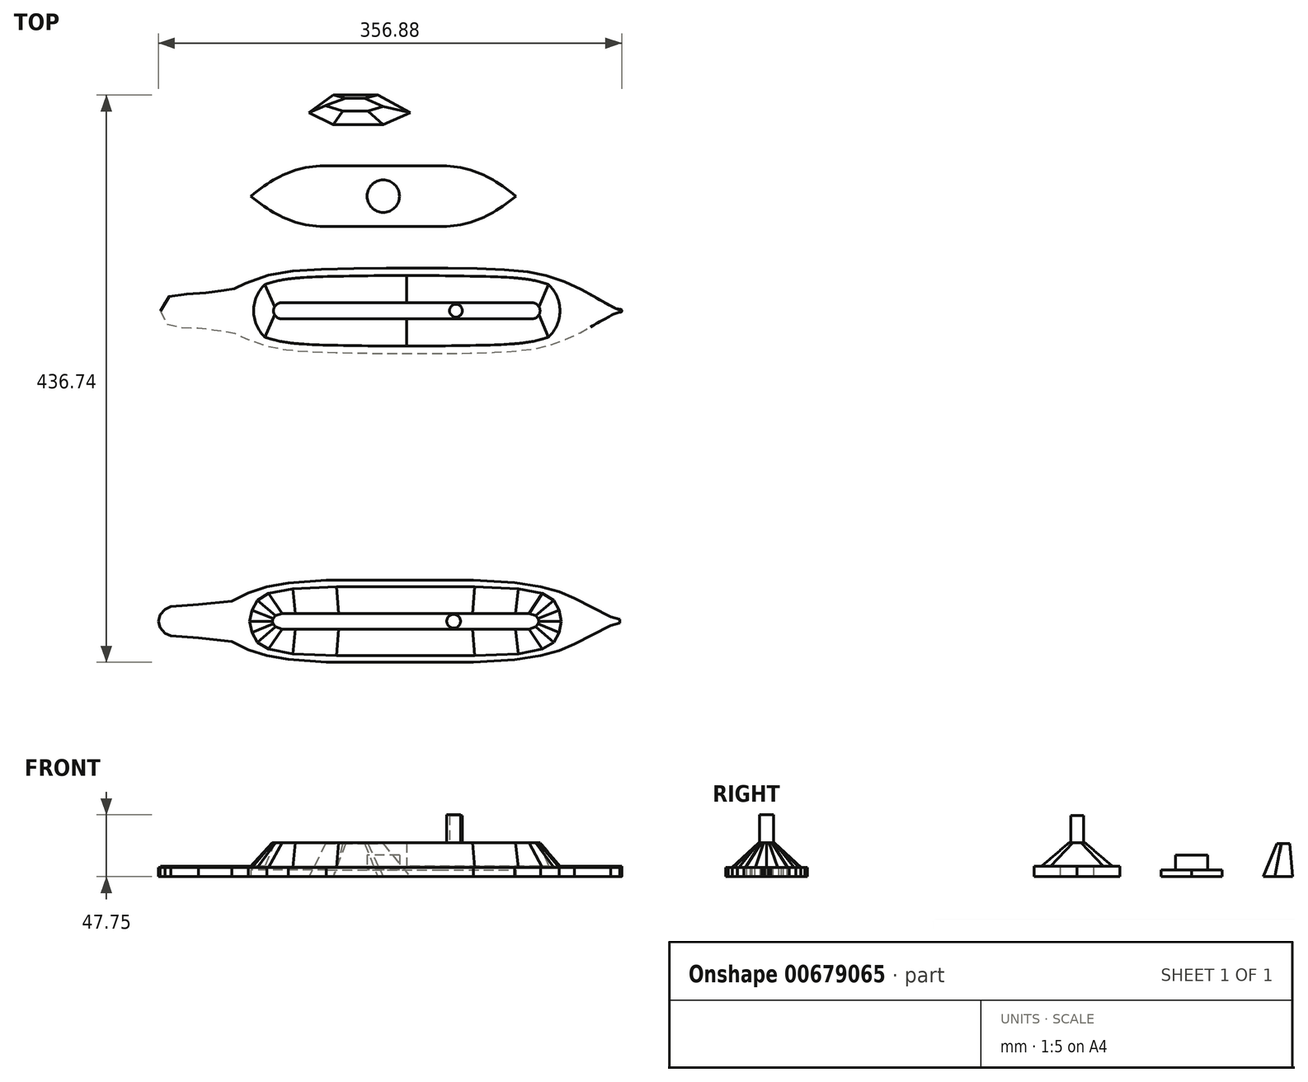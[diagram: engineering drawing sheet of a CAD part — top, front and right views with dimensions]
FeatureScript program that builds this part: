
annotation { "Feature Type Name" : "Feature", "Feature Type Description" : "" }
export const myFeature = defineFeature(function(context is Context, id is Id, definition is map)
    precondition{}
    {
        {
            var Q0;
            Q0=qCreatedBy(makeId("Top.planeOp"),FACE);
            var sketch = newSketch(context, id + "F0", { "sketchPlane" : qUnion([Q0])});
            skLineSegment(sketch, "E0", {"start": v(-42.94, 23.43) * mm, "end": v(0, 23.43) * mm});
            skFitSpline(sketch, "E1", {"points": [v(-42.94, 23.43) * mm, v(-102.11, 0) * mm], "startDerivative": vector(-68.76, 0) * mm, "endDerivative": vector(-60.63, -49.68) * mm});
            skLineSegment(sketch, "E2", {"start": v(-37.52, 23.43) * mm, "end": v(-119.82, 23.43) * mm, "construction": true});
            skLineSegment(sketch, "E3.MirrorCS", {"start": v(-42.94, -23.43) * mm, "end": v(0, -23.43) * mm});
            skFitSpline(sketch, "E4.MirrorCS", {"points": [v(-42.94, -23.43) * mm, v(-102.11, 0) * mm], "startDerivative": vector(-68.76, 0) * mm, "endDerivative": vector(-60.63, 49.68) * mm});
            skLineSegment(sketch, "E5.MirrorCS", {"start": v(42.94, 23.43) * mm, "end": v(0, 23.43) * mm});
            skFitSpline(sketch, "E6.MirrorCS", {"points": [v(42.94, 23.43) * mm, v(102.11, 0) * mm], "startDerivative": vector(68.76, 0) * mm, "endDerivative": vector(60.63, -49.68) * mm});
            skFitSpline(sketch, "E7.MirrorCS", {"points": [v(42.94, -23.43) * mm, v(102.11, 0) * mm], "startDerivative": vector(68.76, 0) * mm, "endDerivative": vector(60.63, 49.68) * mm});
            skLineSegment(sketch, "E8.MirrorCS", {"start": v(42.94, -23.43) * mm, "end": v(0, -23.43) * mm});
            skSolve(sketch);
        }
        {
            var Q0;
            Q0=makeQuery(id+"F0.imprint","IMPRINT",FACE,{"disambiguationData":[TD([[makeQuery(id+"F0.imprint","IMPRINT",EDGE,{"derivedFrom":sQuery(id+"F0.wireOp",EDGE,"E0")}),-1.0]])]});
            extrude(context, id + "F1", {"entities" : qUnion([Q0]), "depth" : 5.08 * mm, "offsetDistance" : 25.4 * mm});
        }
        {
            var Q0;
            Q0=makeQuery(id+"F1.opExtrude","CAP_FACE",FACE,{"disambiguationData":[OSD([sQuery(id+"F0.wireOp",EDGE,"E0"),sQuery(id+"F0.wireOp",EDGE,"E1"),sQuery(id+"F0.wireOp",EDGE,"E3.MirrorCS"),sQuery(id+"F0.wireOp",EDGE,"E4.MirrorCS"),sQuery(id+"F0.wireOp",EDGE,"E5.MirrorCS"),sQuery(id+"F0.wireOp",EDGE,"E6.MirrorCS"),sQuery(id+"F0.wireOp",EDGE,"E7.MirrorCS"),sQuery(id+"F0.wireOp",EDGE,"E8.MirrorCS")])],"isStart":false});
            var sketch = newSketch(context, id + "F2", { "sketchPlane" : qUnion([Q0])});
            skCircle(sketch, "E9", {"center": v(0, 0) * mm, "radius": 12.49 * mm});
            skSolve(sketch);
        }
        {
            var Q0;
            Q0=makeQuery(id+"F2.imprint","IMPRINT",FACE,{"disambiguationData":[TD([[makeQuery(id+"F2.imprint","IMPRINT",EDGE,{"derivedFrom":sQuery(id+"F2.wireOp",EDGE,"E9")}),1.0]])]});
            extrude(context, id + "F3", {"entities" : qUnion([Q0]), "operationType" : NewBodyOperationType.ADD, "depth" : 11.68 * mm, "offsetDistance" : 25.4 * mm});
        }
        {
            var Q0;
            Q0=qCreatedBy(makeId("Top.planeOp"),FACE);
            var sketch = newSketch(context, id + "F4", { "sketchPlane" : qUnion([Q0])});
            skLineSegment(sketch, "E10", {"start": v(-71.94, -45.48) * mm, "end": v(-71.94, -186.72) * mm, "construction": true});
            skLineSegment(sketch, "E11", {"start": v(108.08, -39.14) * mm, "end": v(108.08, -186.72) * mm, "construction": true});
            skLineSegment(sketch, "E12", {"start": v(-197.77, -88.3) * mm, "end": v(328.2, -88.3) * mm, "construction": true});
            skFitSpline(sketch, "E13", {"points": [v(-171.65, -88.3) * mm, v(-163.55, -76.65) * mm, v(-146.07, -75.28) * mm, v(-127.86, -73.29) * mm, v(-116.2, -71.5) * mm, v(-114.9, -71.28) * mm, v(-113.7, -70.6) * mm, v(-93.72, -62.34) * mm, v(-61.63, -57.06) * mm, v(-9.38, -55.61) * mm, v(41.39, -55.4) * mm, v(84.93, -56.24) * mm, v(114.66, -58.75) * mm, v(131.08, -62.76) * mm, v(149.8, -70.54) * mm, v(159.24, -75.62) * mm, v(168.52, -80.9) * mm, v(175.32, -84.67) * mm, v(180.3, -86.82) * mm, v(183.42, -87.51) * mm, v(183.64, -88.3) * mm], "startDerivative": vector(0, 395.34) * mm, "endDerivative": vector(-3.7, -98.79) * mm});
            skLineSegment(sketch, "E14", {"start": v(-171.65, -79.57) * mm, "end": v(-171.65, -98.9) * mm, "construction": true});
            skFitSpline(sketch, "E15.MirrorCS", {"points": [v(-171.65, -88.3) * mm, v(-163.55, -99.94) * mm, v(-146.07, -101.3) * mm, v(-127.86, -103.3) * mm, v(-116.2, -105.09) * mm, v(-114.9, -105.31) * mm, v(-113.7, -106) * mm, v(-93.72, -114.25) * mm, v(-61.63, -119.53) * mm, v(-9.38, -120.98) * mm, v(41.39, -121.2) * mm, v(84.93, -120.35) * mm, v(114.66, -117.84) * mm, v(131.08, -113.83) * mm, v(149.8, -106.05) * mm, v(159.24, -100.97) * mm, v(168.52, -95.69) * mm, v(175.32, -91.92) * mm, v(180.3, -89.77) * mm, v(183.42, -89.08) * mm, v(183.64, -88.3) * mm], "startDerivative": vector(0, -395.34) * mm, "endDerivative": vector(-3.7, 98.79) * mm});
            skSolve(sketch);
        }
        {
            var Q0;
            Q0=makeQuery(id+"F4.imprint","IMPRINT",FACE,{"disambiguationData":[TD([[makeQuery(id+"F4.imprint","IMPRINT",EDGE,{"derivedFrom":sQuery(id+"F4.wireOp",EDGE,"E13")}),-1.0]])]});
            extrude(context, id + "F5", {"entities" : qUnion([Q0]), "depth" : 8.13 * mm, "offsetDistance" : 25.4 * mm});
        }
        {
            var Q0;
            Q0=makeQuery(id+"F5.opExtrude","CAP_FACE",FACE,{"disambiguationData":[OSD([sQuery(id+"F4.wireOp",EDGE,"E13"),sQuery(id+"F4.wireOp",EDGE,"E15.MirrorCS")])],"isStart":false});
            var sketch = newSketch(context, id + "F6", { "sketchPlane" : qUnion([Q0])});
            skLineSegment(sketch, "E16.0", {"start": v(-71.94, -45.48) * mm, "end": v(-71.94, -186.72) * mm, "construction": true});
            skLineSegment(sketch, "E17.0", {"start": v(108.08, -39.14) * mm, "end": v(108.08, -186.72) * mm, "construction": true});
            skLineSegment(sketch, "E18.0", {"start": v(-197.77, -88.3) * mm, "end": v(328.2, -88.3) * mm, "construction": true});
            skArc(sketch, "E19", {"start": v(-60.92, -62.61) * mm, "mid": v(-99.9, -88.3) * mm, "end": v(-60.92, -113.98) * mm});
            skArc(sketch, "E20", {"start": v(97.06, -113.98) * mm, "mid": v(102.46, -115.67) * mm, "end": v(108.08, -116.24) * mm});
            skFitSpline(sketch, "E21", {"points": [v(-109.29, -75.39) * mm, v(-83.95, -65.87) * mm, v(-65.76, -63) * mm, v(-41.52, -61.82) * mm, v(18.07, -61.25) * mm], "startDerivative": vector(81.3, 42.56) * mm, "endDerivative": vector(39.77, -2.18) * mm});
            skLineSegment(sketch, "E22", {"start": v(18.07, -51.14) * mm, "end": v(18.07, -141.86) * mm, "construction": true});
            skLineSegment(sketch, "E23", {"start": v(-71.94, -51.14) * mm, "end": v(108.08, -51.14) * mm, "construction": true});
            skFitSpline(sketch, "E24.MirrorCS", {"points": [v(145.42, -75.39) * mm, v(120.09, -65.87) * mm, v(101.9, -63) * mm, v(77.66, -61.82) * mm, v(18.07, -61.25) * mm], "startDerivative": vector(-81.3, 42.56) * mm, "endDerivative": vector(-39.77, -2.18) * mm});
            skLineSegment(sketch, "E25.MirrorCS", {"start": v(233.9, -88.3) * mm, "end": v(-292.06, -88.3) * mm, "construction": true});
            skFitSpline(sketch, "E26.MirrorCS", {"points": [v(-109.29, -101.2) * mm, v(-83.95, -110.72) * mm, v(-65.76, -113.6) * mm, v(-41.52, -114.77) * mm, v(18.07, -115.34) * mm], "startDerivative": vector(81.3, -42.56) * mm, "endDerivative": vector(39.77, 2.18) * mm});
            skFitSpline(sketch, "E27.MirrorCS", {"points": [v(145.42, -101.2) * mm, v(120.09, -110.72) * mm, v(101.9, -113.6) * mm, v(77.66, -114.77) * mm, v(18.07, -115.34) * mm], "startDerivative": vector(-81.3, -42.56) * mm, "endDerivative": vector(-39.77, 2.18) * mm});
            skArc(sketch, "E28.trimOffspring", {"start": v(108.08, -116.24) * mm, "mid": v(135.46, -82.67) * mm, "end": v(97.06, -62.61) * mm});
            skArc(sketch, "E29.trimOffspring", {"start": v(108.08, -60.35) * mm, "mid": v(102.46, -60.92) * mm, "end": v(97.06, -62.61) * mm});
            skLineSegment(sketch, "E30", {"start": v(145.42, -75.39) * mm, "end": v(145.42, -101.2) * mm});
            skLineSegment(sketch, "E31", {"start": v(-109.29, -75.39) * mm, "end": v(-109.29, -101.2) * mm});
            skSolve(sketch);
        }
        {
            var Q0;
            Q0=makeQuery(id+"F5.opExtrude","CAP_FACE",FACE,{"disambiguationData":[OSD([sQuery(id+"F4.wireOp",EDGE,"E13"),sQuery(id+"F4.wireOp",EDGE,"E15.MirrorCS")])],"isStart":false});
            cPlane(context, id + "F7", {"entities" : qUnion([Q0]), "cplaneType" : CPlaneType.OFFSET, "offset" : 18.03 * mm, "width" : 152.4 * mm, "height" : 152.4 * mm});
        }
        {
            var Q0;
            Q0=qCreatedBy(id+"F7.planeOp",FACE);
            var sketch = newSketch(context, id + "F8", { "sketchPlane" : qUnion([Q0])});
            skLineSegment(sketch, "E32.0", {"start": v(-197.77, -88.3) * mm, "end": v(328.2, -88.3) * mm, "construction": true});
            skArc(sketch, "E33", {"start": v(-78.37, -82.08) * mm, "mid": v(-84.59, -88.3) * mm, "end": v(-78.37, -94.5) * mm});
            skLineSegment(sketch, "E34.0", {"start": v(18.07, -51.14) * mm, "end": v(18.07, -141.86) * mm, "construction": true});
            skArc(sketch, "E35.MirrorC", {"start": v(114.51, -82.08) * mm, "mid": v(120.73, -88.3) * mm, "end": v(114.51, -94.5) * mm});
            skLineSegment(sketch, "E36.bottom", {"start": v(-78.37, -82.08) * mm, "end": v(114.51, -82.08) * mm});
            skLineSegment(sketch, "E36.top", {"start": v(-78.37, -94.5) * mm, "end": v(114.51, -94.5) * mm});
            skSolve(sketch);
        }
        {
            var Q0;
            Q0=sQuery(id+"F6.wireOp",VERTEX,"E21.1.internal");
            var Q1;
            Q1=sQuery(id+"F8.wireOp",VERTEX,"E33.start");
            var Q2;
            Q2=sQuery(id+"F6.wireOp",VERTEX,"E26.MirrorCS.1.internal");
            cPlane(context, id + "F9", {"entities" : qUnion([Q0, Q1, Q2]), "cplaneType" : CPlaneType.THREE_POINT, "offset" : 25.4 * mm, "width" : 152.4 * mm, "height" : 152.4 * mm});
        }
        {
            var Q0;
            Q0=qCreatedBy(id+"F9.planeOp",FACE);
            var sketch = newSketch(context, id + "F10", { "sketchPlane" : qUnion([Q0])});
            skLineSegment(sketch, "E37", {"start": v(94.5, 1.85) * mm, "end": v(110.72, -17.02) * mm});
            skLineSegment(sketch, "E38", {"start": v(82.08, 1.85) * mm, "end": v(65.87, -17.02) * mm});
            skSolve(sketch);
        }
        {
            var Q0;
            Q0=sQuery(id+"F8.wireOp",VERTEX,"E36.bottom.end");
            var Q1;
            Q1=sQuery(id+"F6.wireOp",VERTEX,"E24.MirrorCS.1.internal");
            var Q2;
            Q2=sQuery(id+"F6.wireOp",VERTEX,"E27.MirrorCS.1.internal");
            cPlane(context, id + "F11", {"entities" : qUnion([Q0, Q1, Q2]), "cplaneType" : CPlaneType.THREE_POINT, "offset" : 25.4 * mm, "width" : 152.4 * mm, "height" : 152.4 * mm});
        }
        {
            var Q0;
            Q0=qCreatedBy(id+"F11.planeOp",FACE);
            var sketch = newSketch(context, id + "F12", { "sketchPlane" : qUnion([Q0])});
            skLineSegment(sketch, "E39", {"start": v(-110.72, -27.7) * mm, "end": v(-94.5, -8.82) * mm});
            skLineSegment(sketch, "E40", {"start": v(-82.08, -8.82) * mm, "end": v(-65.87, -27.7) * mm});
            skSolve(sketch);
        }
        {
            var Q1;
            Q1=makeQuery(id+"F8.imprint","IMPRINT",FACE,{"disambiguationData":[TD([[makeQuery(id+"F8.imprint","IMPRINT",EDGE,{"derivedFrom":sQuery(id+"F8.wireOp",EDGE,"E33")}),1.0]])]});
            var Q2;
            {var subQ4=sQuery(id+"F6.wireOp",EDGE,"E21");var subQ5=sQuery(id+"F6.wireOp",EDGE,"E19");var subQ7=makeQuery(id+"F6.imprint","INTERSECT",VERTEX,{"disambiguationData":[OD(1.0)],"derivedFrom":[subQ5,subQ4]});Q2=makeQuery(id+"F6.imprint","IMPRINT",FACE,{"disambiguationData":[TD([[makeQuery(id+"F6.imprint","IMPRINT",EDGE,{"disambiguationData":[TD([[subQ7,-1.0]])],"derivedFrom":subQ5}),1.0]])]});}
            var Q3;
            Q3=sQuery(id+"F12.wireOp",EDGE,"E39");
            var Q4;
            Q4=sQuery(id+"F12.wireOp",EDGE,"E40");
            var Q5;
            Q5=sQuery(id+"F10.wireOp",EDGE,"E37");
            var Q6;
            Q6=sQuery(id+"F10.wireOp",EDGE,"E38");
            loft(context, id + "F13", {"operationType" : NewBodyOperationType.ADD, "addGuides" : true, "sheetProfilesArray" : [{ "sheetProfileEntities" : qUnion([Q1]) }, { "sheetProfileEntities" : qUnion([Q2]) }], "guidesArray" : [{ "guideEntities" : qUnion([Q3]), "guideDerivativeType" : LoftGuideDerivativeType.DEFAULT, "guideDerivativeMagnitude" : 1 }, { "guideEntities" : qUnion([Q4]), "guideDerivativeType" : LoftGuideDerivativeType.DEFAULT, "guideDerivativeMagnitude" : 1 }, { "guideEntities" : qUnion([Q5]), "guideDerivativeType" : LoftGuideDerivativeType.DEFAULT, "guideDerivativeMagnitude" : 1 }, { "guideEntities" : qUnion([Q6]), "guideDerivativeType" : LoftGuideDerivativeType.DEFAULT, "guideDerivativeMagnitude" : 1 }]});
        }
        {
            var Q0;
            Q0=makeQuery(id+"F8.imprint","IMPRINT",FACE,{"disambiguationData":[TD([[makeQuery(id+"F8.imprint","IMPRINT",EDGE,{"derivedFrom":sQuery(id+"F8.wireOp",EDGE,"E33")}),1.0]])]});
            var sketch = newSketch(context, id + "F14", { "sketchPlane" : qUnion([Q0])});
            skCircle(sketch, "E41", {"center": v(55.96, -88.24) * mm, "radius": 4.95 * mm});
            skSolve(sketch);
        }
        {
            var Q0;
            Q0=makeQuery(id+"F14.imprint","IMPRINT",FACE,{"disambiguationData":[TD([[makeQuery(id+"F14.imprint","IMPRINT",EDGE,{"derivedFrom":sQuery(id+"F14.wireOp",EDGE,"E41")}),1.0]])]});
            extrude(context, id + "F15", {"entities" : qUnion([Q0]), "operationType" : NewBodyOperationType.ADD, "depth" : 21.08 * mm, "offsetDistance" : 25.4 * mm});
        }
        {
            var Q0;
            Q0=qCreatedBy(makeId("Top.planeOp"),FACE);
            var sketch = newSketch(context, id + "F16", { "sketchPlane" : qUnion([Q0])});
            skLineSegment(sketch, "E42", {"start": v(-57.17, 64.26) * mm, "end": v(-38.38, 77.84) * mm});
            skLineSegment(sketch, "E43", {"start": v(-38.38, 77.84) * mm, "end": v(-4.18, 77.84) * mm});
            skLineSegment(sketch, "E44", {"start": v(-4.18, 77.84) * mm, "end": v(20.88, 64.26) * mm});
            skLineSegment(sketch, "E45", {"start": v(20.88, 64.26) * mm, "end": v(0, 55.13) * mm});
            skLineSegment(sketch, "E46", {"start": v(0, 55.13) * mm, "end": v(-38.38, 55.13) * mm});
            skLineSegment(sketch, "E47", {"start": v(-38.38, 55.13) * mm, "end": v(-57.17, 64.26) * mm});
            skSolve(sketch);
        }
        {
            var Q0;
            Q0=makeQuery(id+"F16.imprint","IMPRINT",FACE,{"disambiguationData":[TD([[makeQuery(id+"F16.imprint","IMPRINT",EDGE,{"derivedFrom":sQuery(id+"F16.wireOp",EDGE,"E42")}),-1.0]])]});
            cPlane(context, id + "F17", {"entities" : qUnion([Q0]), "cplaneType" : CPlaneType.OFFSET, "offset" : 25.4 * mm, "width" : 152.4 * mm, "height" : 152.4 * mm});
        }
        {
            var Q0;
            Q0=qCreatedBy(id+"F17.planeOp",FACE);
            var sketch = newSketch(context, id + "F18", { "sketchPlane" : qUnion([Q0])});
            skLineSegment(sketch, "E48", {"start": v(-29.05, 75.27) * mm, "end": v(-44.41, 69.77) * mm});
            skLineSegment(sketch, "E49", {"start": v(-44.41, 69.77) * mm, "end": v(-31.25, 65.58) * mm});
            skLineSegment(sketch, "E50", {"start": v(-31.25, 65.58) * mm, "end": v(-11.87, 65.58) * mm});
            skLineSegment(sketch, "E51", {"start": v(-11.87, 65.58) * mm, "end": v(0, 68.93) * mm});
            skLineSegment(sketch, "E52", {"start": v(0, 68.93) * mm, "end": v(-14.39, 75.38) * mm});
            skLineSegment(sketch, "E53", {"start": v(-14.39, 75.38) * mm, "end": v(-29.05, 75.27) * mm});
            skSolve(sketch);
        }
        {
            var Q0;
            Q0=makeQuery(id+"F18.imprint","IMPRINT",FACE,{"disambiguationData":[TD([[makeQuery(id+"F18.imprint","IMPRINT",EDGE,{"derivedFrom":sQuery(id+"F18.wireOp",EDGE,"E48")}),1.0]])]});
            var Q1;
            Q1=makeQuery(id+"F16.imprint","IMPRINT",FACE,{"disambiguationData":[TD([[makeQuery(id+"F16.imprint","IMPRINT",EDGE,{"derivedFrom":sQuery(id+"F16.wireOp",EDGE,"E42")}),-1.0]])]});
            loft(context, id + "F19", {"sheetProfilesArray" : [{ "sheetProfileEntities" : qUnion([Q0]) }, { "sheetProfileEntities" : qUnion([Q1]) }]});
        }
        {
            var Q0;
            Q0=qCreatedBy(makeId("Top.planeOp"),FACE);
            var sketch = newSketch(context, id + "F20", { "sketchPlane" : qUnion([Q0])});
            skLineSegment(sketch, "E54", {"start": v(-176.14, -327.4) * mm, "end": v(194.44, -327.4) * mm, "construction": true});
            skLineSegment(sketch, "E55", {"start": v(-173.24, -327.4) * mm, "end": v(-171.72, -322.5) * mm});
            skLineSegment(sketch, "E56", {"start": v(-171.72, -322.5) * mm, "end": v(-167.99, -318.24) * mm});
            skLineSegment(sketch, "E57", {"start": v(-167.99, -318.24) * mm, "end": v(-163.53, -316.13) * mm});
            skLineSegment(sketch, "E58", {"start": v(-163.53, -316.13) * mm, "end": v(-142.23, -314.57) * mm});
            skLineSegment(sketch, "E59", {"start": v(-142.23, -314.57) * mm, "end": v(-116.78, -311.82) * mm});
            skLineSegment(sketch, "E60", {"start": v(-116.78, -311.82) * mm, "end": v(-104, -305.48) * mm});
            skLineSegment(sketch, "E61", {"start": v(-104, -305.48) * mm, "end": v(-89.78, -300.98) * mm});
            skLineSegment(sketch, "E62", {"start": v(-89.78, -300.98) * mm, "end": v(-73.04, -298.02) * mm});
            skLineSegment(sketch, "E63", {"start": v(-73.04, -298.02) * mm, "end": v(-43.76, -295.9) * mm});
            skLineSegment(sketch, "E64", {"start": v(-43.76, -295.9) * mm, "end": v(69.46, -295.9) * mm});
            skLineSegment(sketch, "E65", {"start": v(69.46, -295.9) * mm, "end": v(101.23, -297.81) * mm});
            skLineSegment(sketch, "E66", {"start": v(101.23, -297.81) * mm, "end": v(121.16, -300.98) * mm});
            skLineSegment(sketch, "E67", {"start": v(121.16, -300.98) * mm, "end": v(135.46, -304.73) * mm});
            skLineSegment(sketch, "E68", {"start": v(135.46, -304.73) * mm, "end": v(147.24, -309.84) * mm});
            skLineSegment(sketch, "E69", {"start": v(147.24, -309.84) * mm, "end": v(157.53, -315.1) * mm});
            skLineSegment(sketch, "E70", {"start": v(157.53, -315.1) * mm, "end": v(175.12, -324.06) * mm});
            skLineSegment(sketch, "E71", {"start": v(175.12, -324.06) * mm, "end": v(182.27, -325.93) * mm});
            skLineSegment(sketch, "E72", {"start": v(182.27, -325.93) * mm, "end": v(182.27, -327.4) * mm});
            skLineSegment(sketch, "E73.MirrorCS", {"start": v(-73.04, -356.78) * mm, "end": v(-43.76, -358.9) * mm});
            skLineSegment(sketch, "E74.MirrorCS", {"start": v(-89.78, -353.82) * mm, "end": v(-73.04, -356.78) * mm});
            skLineSegment(sketch, "E75.MirrorCS", {"start": v(-104, -349.32) * mm, "end": v(-89.78, -353.82) * mm});
            skLineSegment(sketch, "E76.MirrorCS", {"start": v(-116.78, -342.98) * mm, "end": v(-104, -349.32) * mm});
            skLineSegment(sketch, "E77.MirrorCS", {"start": v(-142.23, -340.23) * mm, "end": v(-116.78, -342.98) * mm});
            skLineSegment(sketch, "E78.MirrorCS", {"start": v(-163.53, -338.67) * mm, "end": v(-142.23, -340.23) * mm});
            skLineSegment(sketch, "E79.MirrorCS", {"start": v(-167.99, -336.56) * mm, "end": v(-163.53, -338.67) * mm});
            skLineSegment(sketch, "E80.MirrorCS", {"start": v(-173.24, -327.4) * mm, "end": v(-171.72, -332.3) * mm});
            skLineSegment(sketch, "E81.MirrorCS", {"start": v(-171.72, -332.3) * mm, "end": v(-167.99, -336.56) * mm});
            skLineSegment(sketch, "E82.MirrorCS", {"start": v(-43.76, -358.9) * mm, "end": v(69.46, -358.9) * mm});
            skLineSegment(sketch, "E83.MirrorCS", {"start": v(69.46, -358.9) * mm, "end": v(101.23, -357) * mm});
            skLineSegment(sketch, "E84.MirrorCS", {"start": v(101.23, -357) * mm, "end": v(121.16, -353.82) * mm});
            skLineSegment(sketch, "E85.MirrorCS", {"start": v(121.16, -353.82) * mm, "end": v(135.46, -350.07) * mm});
            skLineSegment(sketch, "E86.MirrorCS", {"start": v(135.46, -350.07) * mm, "end": v(147.24, -344.96) * mm});
            skLineSegment(sketch, "E87.MirrorCS", {"start": v(147.24, -344.96) * mm, "end": v(157.53, -339.7) * mm});
            skLineSegment(sketch, "E88.MirrorCS", {"start": v(157.53, -339.7) * mm, "end": v(175.12, -330.74) * mm});
            skLineSegment(sketch, "E89.MirrorCS", {"start": v(175.12, -330.74) * mm, "end": v(182.27, -328.87) * mm});
            skLineSegment(sketch, "E90.MirrorCS", {"start": v(182.27, -328.87) * mm, "end": v(182.27, -327.4) * mm});
            skSolve(sketch);
        }
        {
            var Q0;
            Q0=makeQuery(id+"F20.imprint","IMPRINT",FACE,{"disambiguationData":[TD([[makeQuery(id+"F20.imprint","IMPRINT",EDGE,{"derivedFrom":sQuery(id+"F20.wireOp",EDGE,"E55")}),-1.0]])]});
            extrude(context, id + "F21", {"entities" : qUnion([Q0]), "depth" : 7.11 * mm, "offsetDistance" : 25.4 * mm});
        }
        {
            var Q0;
            Q0=makeQuery(id+"F21.opExtrude","CAP_FACE",FACE,{"disambiguationData":[OSD([sQuery(id+"F20.wireOp",EDGE,"E55"),sQuery(id+"F20.wireOp",EDGE,"E56"),sQuery(id+"F20.wireOp",EDGE,"E57"),sQuery(id+"F20.wireOp",EDGE,"E58"),sQuery(id+"F20.wireOp",EDGE,"E59"),sQuery(id+"F20.wireOp",EDGE,"E60"),sQuery(id+"F20.wireOp",EDGE,"E61"),sQuery(id+"F20.wireOp",EDGE,"E62"),sQuery(id+"F20.wireOp",EDGE,"E63"),sQuery(id+"F20.wireOp",EDGE,"E64"),sQuery(id+"F20.wireOp",EDGE,"E65"),sQuery(id+"F20.wireOp",EDGE,"E66"),sQuery(id+"F20.wireOp",EDGE,"E67"),sQuery(id+"F20.wireOp",EDGE,"E68"),sQuery(id+"F20.wireOp",EDGE,"E69"),sQuery(id+"F20.wireOp",EDGE,"E70"),sQuery(id+"F20.wireOp",EDGE,"E71"),sQuery(id+"F20.wireOp",EDGE,"E72"),sQuery(id+"F20.wireOp",EDGE,"E73.MirrorCS"),sQuery(id+"F20.wireOp",EDGE,"E74.MirrorCS"),sQuery(id+"F20.wireOp",EDGE,"E75.MirrorCS"),sQuery(id+"F20.wireOp",EDGE,"E76.MirrorCS"),sQuery(id+"F20.wireOp",EDGE,"E77.MirrorCS"),sQuery(id+"F20.wireOp",EDGE,"E78.MirrorCS"),sQuery(id+"F20.wireOp",EDGE,"E79.MirrorCS"),sQuery(id+"F20.wireOp",EDGE,"E80.MirrorCS"),sQuery(id+"F20.wireOp",EDGE,"E81.MirrorCS"),sQuery(id+"F20.wireOp",EDGE,"E82.MirrorCS"),sQuery(id+"F20.wireOp",EDGE,"E83.MirrorCS"),sQuery(id+"F20.wireOp",EDGE,"E84.MirrorCS"),sQuery(id+"F20.wireOp",EDGE,"E85.MirrorCS"),sQuery(id+"F20.wireOp",EDGE,"E86.MirrorCS"),sQuery(id+"F20.wireOp",EDGE,"E87.MirrorCS"),sQuery(id+"F20.wireOp",EDGE,"E88.MirrorCS"),sQuery(id+"F20.wireOp",EDGE,"E89.MirrorCS"),sQuery(id+"F20.wireOp",EDGE,"E90.MirrorCS")])],"isStart":false});
            var sketch = newSketch(context, id + "F22", { "sketchPlane" : qUnion([Q0])});
            skLineSegment(sketch, "E91.0", {"start": v(-176.14, -327.4) * mm, "end": v(194.44, -327.4) * mm, "construction": true});
            skLineSegment(sketch, "E92", {"start": v(-102.83, -327.4) * mm, "end": v(-101.04, -318.78) * mm});
            skLineSegment(sketch, "E93", {"start": v(-101.04, -318.78) * mm, "end": v(-96.91, -311.25) * mm});
            skLineSegment(sketch, "E94", {"start": v(-96.91, -311.25) * mm, "end": v(-88.25, -306) * mm});
            skLineSegment(sketch, "E95", {"start": v(-88.25, -306) * mm, "end": v(-69.62, -302.33) * mm});
            skLineSegment(sketch, "E96", {"start": v(-69.62, -302.33) * mm, "end": v(-36.05, -300.8) * mm});
            skLineSegment(sketch, "E97", {"start": v(-36.05, -300.8) * mm, "end": v(17.15, -300.8) * mm});
            skLineSegment(sketch, "E98", {"start": v(-80.15, -322.04) * mm, "end": v(-80.15, -332.3) * mm, "construction": true});
            skLineSegment(sketch, "E99", {"start": v(114.45, -320.75) * mm, "end": v(114.45, -335.4) * mm, "construction": true});
            skLineSegment(sketch, "E100", {"start": v(-80.15, -325.1) * mm, "end": v(114.45, -325.1) * mm, "construction": true});
            skPoint(sketch, "E101", {"position": v(17.15, -325.1) * mm});
            skLineSegment(sketch, "E102", {"start": v(17.15, -289.6) * mm, "end": v(17.15, -325.1) * mm, "construction": true});
            skLineSegment(sketch, "E103.MirrorCS", {"start": v(70.35, -300.8) * mm, "end": v(17.15, -300.8) * mm});
            skLineSegment(sketch, "E104.MirrorCS", {"start": v(103.92, -302.33) * mm, "end": v(70.35, -300.8) * mm});
            skLineSegment(sketch, "E105.MirrorCS", {"start": v(122.54, -306) * mm, "end": v(103.92, -302.33) * mm});
            skLineSegment(sketch, "E106.MirrorCS", {"start": v(131.2, -311.25) * mm, "end": v(122.54, -306) * mm});
            skLineSegment(sketch, "E107.MirrorCS", {"start": v(135.34, -318.78) * mm, "end": v(131.2, -311.25) * mm});
            skLineSegment(sketch, "E108.MirrorCS", {"start": v(137.13, -327.4) * mm, "end": v(135.34, -318.78) * mm});
            skLineSegment(sketch, "E109.MirrorCS", {"start": v(-102.83, -327.4) * mm, "end": v(-101.04, -336.02) * mm});
            skLineSegment(sketch, "E110.MirrorCS", {"start": v(-101.04, -336.02) * mm, "end": v(-96.91, -343.56) * mm});
            skLineSegment(sketch, "E111.MirrorCS", {"start": v(-96.91, -343.56) * mm, "end": v(-88.25, -348.8) * mm});
            skLineSegment(sketch, "E112.MirrorCS", {"start": v(-88.25, -348.8) * mm, "end": v(-69.62, -352.47) * mm});
            skLineSegment(sketch, "E113.MirrorCS", {"start": v(-69.62, -352.47) * mm, "end": v(-36.05, -354) * mm});
            skLineSegment(sketch, "E114.MirrorCS", {"start": v(-36.05, -354) * mm, "end": v(17.15, -354) * mm});
            skLineSegment(sketch, "E115.MirrorCS", {"start": v(70.35, -354) * mm, "end": v(17.15, -354) * mm});
            skLineSegment(sketch, "E116.MirrorCS", {"start": v(103.92, -352.47) * mm, "end": v(70.35, -354) * mm});
            skLineSegment(sketch, "E117.MirrorCS", {"start": v(122.54, -348.8) * mm, "end": v(103.92, -352.47) * mm});
            skLineSegment(sketch, "E118.MirrorCS", {"start": v(131.2, -343.56) * mm, "end": v(122.54, -348.8) * mm});
            skLineSegment(sketch, "E119.MirrorCS", {"start": v(135.34, -336.02) * mm, "end": v(131.2, -343.56) * mm});
            skLineSegment(sketch, "E120.MirrorCS", {"start": v(137.13, -327.4) * mm, "end": v(135.34, -336.02) * mm});
            skSolve(sketch);
        }
        {
            var Q0;
            Q0=makeQuery(id+"F22.imprint","IMPRINT",FACE,{"disambiguationData":[TD([[makeQuery(id+"F22.imprint","IMPRINT",EDGE,{"derivedFrom":sQuery(id+"F22.wireOp",EDGE,"E92")}),-1.0]])]});
            cPlane(context, id + "F23", {"entities" : qUnion([Q0]), "cplaneType" : CPlaneType.OFFSET, "offset" : 19.05 * mm, "width" : 152.4 * mm, "height" : 152.4 * mm});
        }
        {
            var Q0;
            Q0=qCreatedBy(id+"F23.planeOp",FACE);
            var sketch = newSketch(context, id + "F24", { "sketchPlane" : qUnion([Q0])});
            skLineSegment(sketch, "E121.0", {"start": v(-176.14, -327.4) * mm, "end": v(194.44, -327.4) * mm, "construction": true});
            skLineSegment(sketch, "E122", {"start": v(-85.57, -327.4) * mm, "end": v(-84.99, -325.32) * mm});
            skLineSegment(sketch, "E123", {"start": v(-84.99, -325.32) * mm, "end": v(-82.98, -323.14) * mm});
            skLineSegment(sketch, "E124", {"start": v(-82.98, -323.14) * mm, "end": v(-78.05, -321.32) * mm});
            skLineSegment(sketch, "E125", {"start": v(-78.05, -321.32) * mm, "end": v(-67.61, -321.32) * mm});
            skLineSegment(sketch, "E126", {"start": v(-67.61, -321.32) * mm, "end": v(-34.53, -321.32) * mm});
            skLineSegment(sketch, "E127", {"start": v(-34.53, -321.32) * mm, "end": v(17.15, -321.32) * mm});
            skLineSegment(sketch, "E128.0", {"start": v(17.15, -289.6) * mm, "end": v(17.15, -325.1) * mm, "construction": true});
            skLineSegment(sketch, "E129.MirrorCS", {"start": v(119.28, -325.32) * mm, "end": v(117.28, -323.14) * mm});
            skLineSegment(sketch, "E130.MirrorCS", {"start": v(117.28, -323.14) * mm, "end": v(112.34, -321.32) * mm});
            skLineSegment(sketch, "E131.MirrorCS", {"start": v(119.87, -327.4) * mm, "end": v(119.28, -325.32) * mm});
            skLineSegment(sketch, "E132.MirrorCS", {"start": v(68.83, -321.32) * mm, "end": v(17.15, -321.32) * mm});
            skLineSegment(sketch, "E133.MirrorCS", {"start": v(101.9, -321.32) * mm, "end": v(68.83, -321.32) * mm});
            skLineSegment(sketch, "E134.MirrorCS", {"start": v(112.34, -321.32) * mm, "end": v(101.9, -321.32) * mm});
            skLineSegment(sketch, "E135.MirrorCS", {"start": v(-85.57, -327.4) * mm, "end": v(-84.99, -329.49) * mm});
            skLineSegment(sketch, "E136.MirrorCS", {"start": v(119.87, -327.4) * mm, "end": v(119.28, -329.49) * mm});
            skLineSegment(sketch, "E137.MirrorCS", {"start": v(-84.99, -329.49) * mm, "end": v(-82.98, -331.66) * mm});
            skLineSegment(sketch, "E138.MirrorCS", {"start": v(117.28, -331.66) * mm, "end": v(112.34, -333.48) * mm});
            skLineSegment(sketch, "E139.MirrorCS", {"start": v(-82.98, -331.66) * mm, "end": v(-78.05, -333.48) * mm});
            skLineSegment(sketch, "E140.MirrorCS", {"start": v(119.28, -329.49) * mm, "end": v(117.28, -331.66) * mm});
            skLineSegment(sketch, "E141.MirrorCS", {"start": v(112.34, -333.48) * mm, "end": v(101.9, -333.48) * mm});
            skLineSegment(sketch, "E142.MirrorCS", {"start": v(101.9, -333.48) * mm, "end": v(68.83, -333.48) * mm});
            skLineSegment(sketch, "E143.MirrorCS", {"start": v(68.83, -333.48) * mm, "end": v(17.15, -333.48) * mm});
            skLineSegment(sketch, "E144.MirrorCS", {"start": v(-67.61, -333.48) * mm, "end": v(-34.53, -333.48) * mm});
            skLineSegment(sketch, "E145.MirrorCS", {"start": v(-78.05, -333.48) * mm, "end": v(-67.61, -333.48) * mm});
            skLineSegment(sketch, "E146.MirrorCS", {"start": v(-34.53, -333.48) * mm, "end": v(17.15, -333.48) * mm});
            skSolve(sketch);
        }
        {
            var Q1;
            Q1=makeQuery(id+"F24.imprint","IMPRINT",FACE,{"disambiguationData":[TD([[makeQuery(id+"F24.imprint","IMPRINT",EDGE,{"derivedFrom":sQuery(id+"F24.wireOp",EDGE,"E122")}),-1.0]])]});
            var Q2;
            Q2=makeQuery(id+"F22.imprint","IMPRINT",FACE,{"disambiguationData":[TD([[makeQuery(id+"F22.imprint","IMPRINT",EDGE,{"derivedFrom":sQuery(id+"F22.wireOp",EDGE,"E92")}),-1.0]])]});
            loft(context, id + "F25", {"sheetProfilesArray" : [{ "sheetProfileEntities" : qUnion([Q1]) }, { "sheetProfileEntities" : qUnion([Q2]) }]});
        }
        {
            var Q0;
            Q0=makeQuery(id+"F25.opLoft","CAP_FACE",FACE,{"disambiguationData":[OSD([makeQuery(id+"F24.imprint","IMPRINT",FACE,{"disambiguationData":[TD([[makeQuery(id+"F24.imprint","IMPRINT",EDGE,{"derivedFrom":sQuery(id+"F24.wireOp",EDGE,"E122")}),-1.0]])]})])],"isStart":true});
            var sketch = newSketch(context, id + "F26", { "sketchPlane" : qUnion([Q0])});
            skLineSegment(sketch, "E147.0", {"start": v(-176.14, -327.4) * mm, "end": v(194.44, -327.4) * mm, "construction": true});
            skCircle(sketch, "E148", {"center": v(54.22, -327.4) * mm, "radius": 5.3 * mm});
            skSolve(sketch);
        }
        {
            var Q0;
            Q0=makeQuery(id+"F26.imprint","IMPRINT",FACE,{"disambiguationData":[TD([[makeQuery(id+"F26.imprint","IMPRINT",EDGE,{"derivedFrom":sQuery(id+"F26.wireOp",EDGE,"E148")}),1.0]])]});
            var Q1;
            Q1=sQuery(id+"F26.wireOp",EDGE,"E148");
            extrude(context, id + "F27", {"entities" : qUnion([Q0]), "operationType" : NewBodyOperationType.ADD, "surfaceEntities" : qUnion([Q1]), "depth" : 21.59 * mm, "offsetDistance" : 25.4 * mm});
        }
    });
